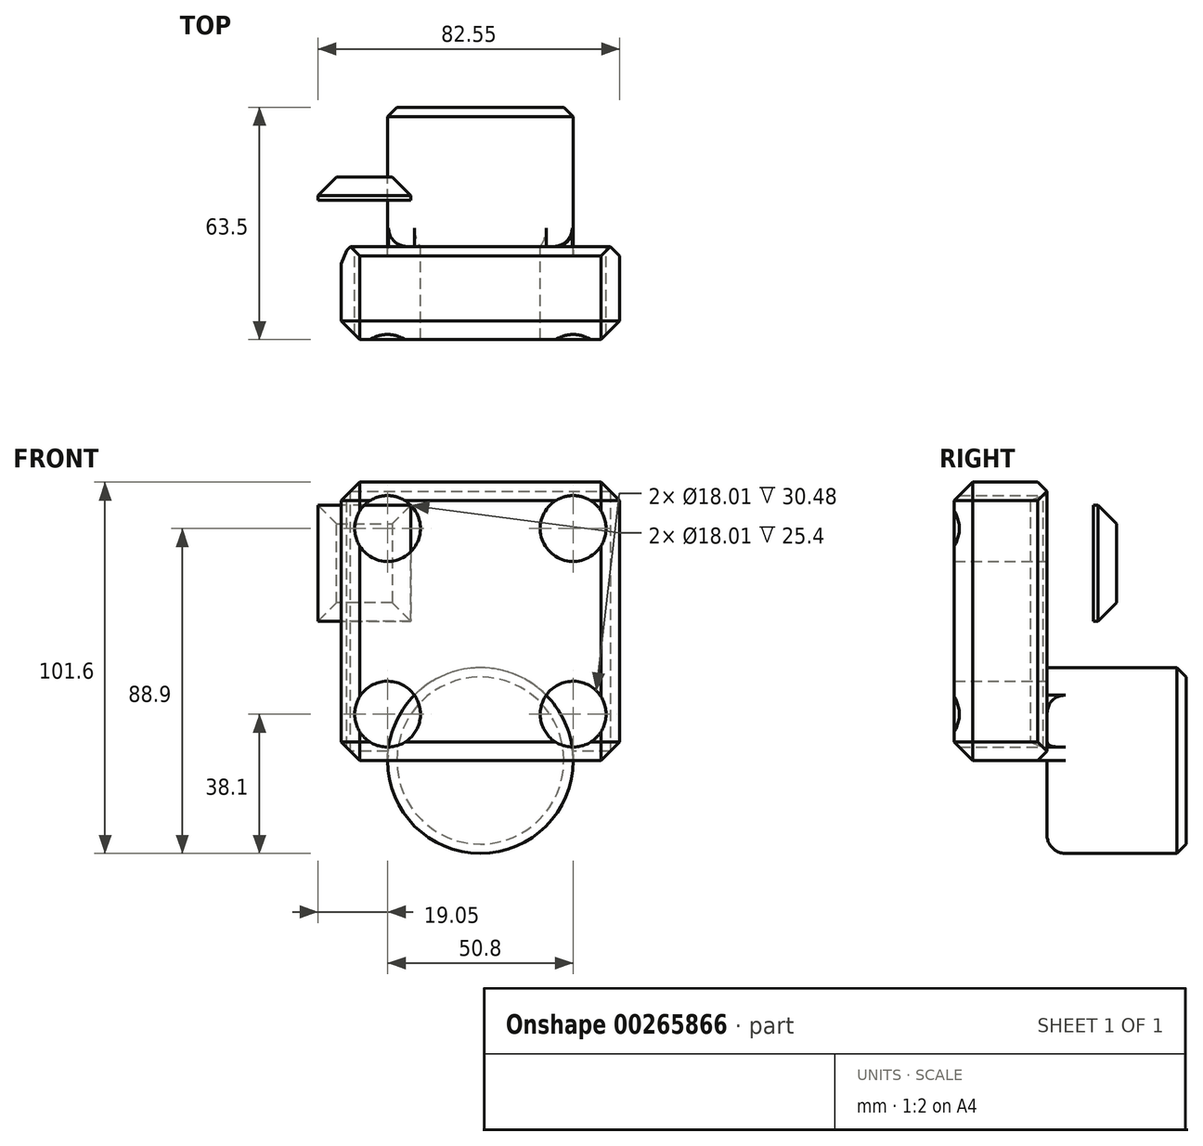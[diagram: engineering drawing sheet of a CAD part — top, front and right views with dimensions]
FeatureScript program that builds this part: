
annotation { "Feature Type Name" : "Feature", "Feature Type Description" : "" }
export const myFeature = defineFeature(function(context is Context, id is Id, definition is map)
    precondition{}
    {
        {
            var Q0;
            Q0=qCreatedBy(makeId("Front.planeOp"),FACE);
            var sketch = newSketch(context, id + "F0", { "sketchPlane" : qUnion([Q0])});
            skLineSegment(sketch, "E0.bottom", {"start": v(-38.1, 38.1) * mm, "end": v(38.1, 38.1) * mm});
            skLineSegment(sketch, "E0.top", {"start": v(-38.1, -38.1) * mm, "end": v(38.1, -38.1) * mm});
            skLineSegment(sketch, "E0.left", {"start": v(-38.1, 38.1) * mm, "end": v(-38.1, -38.1) * mm});
            skLineSegment(sketch, "E0.right", {"start": v(38.1, 38.1) * mm, "end": v(38.1, -38.1) * mm});
            skSolve(sketch);
        }
        {
            var Q0;
            Q0=makeQuery(id+"F0.imprint","IMPRINT",FACE,{"disambiguationData":[TD([[makeQuery(id+"F0.imprint","IMPRINT",EDGE,{"derivedFrom":sQuery(id+"F0.wireOp",EDGE,"E0.bottom")}),-1.0]])]});
            extrude(context, id + "F1", {"entities" : qUnion([Q0]), "oppositeDirection" : true, "depth" : 25.4 * mm});
        }
        {
            var Q0;
            Q0=makeQuery(id+"F1.opExtrude","CAP_FACE",FACE,{"disambiguationData":[OSD([sQuery(id+"F0.wireOp",EDGE,"E0.bottom"),sQuery(id+"F0.wireOp",EDGE,"E0.top"),sQuery(id+"F0.wireOp",EDGE,"E0.left"),sQuery(id+"F0.wireOp",EDGE,"E0.right")])],"isStart":false});
            var sketch = newSketch(context, id + "F2", { "sketchPlane" : qUnion([Q0])});
            skCircle(sketch, "E1", {"center": v(25.4, -25.4) * mm, "radius": 9 * mm});
            skCircle(sketch, "E2", {"center": v(-25.4, -25.4) * mm, "radius": 9 * mm});
            skCircle(sketch, "E3", {"center": v(25.4, 25.4) * mm, "radius": 9 * mm});
            skCircle(sketch, "E4", {"center": v(-25.4, 25.4) * mm, "radius": 9 * mm});
            skSolve(sketch);
        }
        {
            var Q0;
            Q0 = qSketchRegion(id + "F2", true);
            extrude(context, id + "F3", {"entities" : qUnion([Q0]), "operationType" : NewBodyOperationType.REMOVE, "oppositeDirection" : true, "depth" : 25.4 * mm});
        }
        {
            var Q0;
            Q0=makeQuery(id+"F1.opExtrude","SWEPT_FACE",FACE,{"disambiguationData":[OSD([sQuery(id+"F0.wireOp",EDGE,"E0.top")])]});
            var sketch = newSketch(context, id + "F4", { "sketchPlane" : qUnion([Q0])});
            skLineSegment(sketch, "E5.bottom", {"start": v(0, -63.5) * mm, "end": v(-25.4, -63.5) * mm});
            skLineSegment(sketch, "E5.top", {"start": v(0, -25.4) * mm, "end": v(-25.4, -25.4) * mm});
            skLineSegment(sketch, "E5.left", {"start": v(0, -63.5) * mm, "end": v(0, -25.4) * mm});
            skLineSegment(sketch, "E5.right", {"start": v(-25.4, -63.5) * mm, "end": v(-25.4, -25.4) * mm});
            skSolve(sketch);
        }
        {
            var Q0;
            Q0=makeQuery(id+"F4.imprint","IMPRINT",FACE,{"disambiguationData":[TD([[makeQuery(id+"F4.imprint","IMPRINT",EDGE,{"derivedFrom":sQuery(id+"F4.wireOp",EDGE,"E5.bottom")}),-1.0]])]});
            var Q1;
            Q1=sQuery(id+"F4.wireOp",EDGE,"E5.left");
            revolve(context, id + "F5", {"operationType" : NewBodyOperationType.ADD, "entities" : qUnion([Q0]), "axis" : qUnion([Q1]), "revolveType" : RevolveType.FULL});
        }
        {
            var Q0;
            Q0=qCreatedBy(makeId("Top.planeOp"),FACE);
            var sketch = newSketch(context, id + "F6", { "sketchPlane" : qUnion([Q0])});
            skLineSegment(sketch, "E6.bottom", {"start": v(-19.05, 44.45) * mm, "end": v(-44.45, 44.45) * mm});
            skLineSegment(sketch, "E6.top", {"start": v(-19.05, 38.1) * mm, "end": v(-44.45, 38.1) * mm});
            skLineSegment(sketch, "E6.left", {"start": v(-19.05, 44.45) * mm, "end": v(-19.05, 38.1) * mm});
            skLineSegment(sketch, "E6.right", {"start": v(-44.45, 44.45) * mm, "end": v(-44.45, 38.1) * mm});
            skSolve(sketch);
        }
        {
            var Q0;
            Q0 = qSketchRegion(id + "F6", true);
            extrude(context, id + "F7", {"entities" : qUnion([Q0]), "depth" : 31.75 * mm});
        }
        {
            var Q0;
            Q0=makeQuery(id+"F1.opExtrude","CAP_EDGE",EDGE,{"disambiguationData":[OSD([sQuery(id+"F0.wireOp",EDGE,"E0.right")])],"isStart":false});
            var Q1;
            Q1=makeQuery(id+"F1.opExtrude","CAP_EDGE",EDGE,{"disambiguationData":[OSD([sQuery(id+"F0.wireOp",EDGE,"E0.bottom")])],"isStart":false});
            var Q2;
            Q2=makeQuery(id+"F1.opExtrude","CAP_EDGE",EDGE,{"disambiguationData":[OSD([sQuery(id+"F0.wireOp",EDGE,"E0.left")])],"isStart":false});
            var Q3;
            {var subQ0=sQuery(id+"F0.wireOp",EDGE,"E0.left");var subQ1=sQuery(id+"F0.wireOp",EDGE,"E0.top");var subQ2=makeQuery(id+"F1.opExtrude","SWEPT_FACE",FACE,{"disambiguationData":[OSD([subQ1])]});var subQ3=makeQuery(id+"F1.opExtrude","CAP_FACE",FACE,{"disambiguationData":[OSD([sQuery(id+"F0.wireOp",EDGE,"E0.bottom"),subQ1,subQ0,sQuery(id+"F0.wireOp",EDGE,"E0.right")])],"isStart":false});Q3=makeQuery(id+"F5.boolean.opBoolean","SPLIT",EDGE,{"disambiguationData":[topologyDisambiguationEdgeConnected([subQ3,subQ2]),TD([makeQuery(id+"F1.opExtrude","SWEPT_FACE",FACE,{"disambiguationData":[OSD([subQ0])]})])],"derivedFrom":makeQuery(id+"F1.opExtrude","CAP_EDGE",EDGE,{"disambiguationData":[OSD([subQ1])],"isStart":false})});}
            var Q4;
            {var subQ0=sQuery(id+"F0.wireOp",EDGE,"E0.right");var subQ1=sQuery(id+"F0.wireOp",EDGE,"E0.top");var subQ2=makeQuery(id+"F1.opExtrude","SWEPT_FACE",FACE,{"disambiguationData":[OSD([subQ1])]});var subQ3=makeQuery(id+"F1.opExtrude","CAP_FACE",FACE,{"disambiguationData":[OSD([sQuery(id+"F0.wireOp",EDGE,"E0.bottom"),subQ1,sQuery(id+"F0.wireOp",EDGE,"E0.left"),subQ0])],"isStart":false});Q4=makeQuery(id+"F5.boolean.opBoolean","SPLIT",EDGE,{"disambiguationData":[topologyDisambiguationEdgeConnected([subQ3,subQ2]),TD([makeQuery(id+"F1.opExtrude","SWEPT_FACE",FACE,{"disambiguationData":[OSD([subQ0])]})])],"derivedFrom":makeQuery(id+"F1.opExtrude","CAP_EDGE",EDGE,{"disambiguationData":[OSD([subQ1])],"isStart":false})});}
            var Q5;
            Q5=makeQuery(id+"F5.opRevolve","SWEPT_EDGE",EDGE,{"disambiguationData":[OSD([sQuery(id+"F4.wireOp",EDGE,"E5.bottom"),sQuery(id+"F4.wireOp",EDGE,"E5.right")])]});
            chamfer(context, id + "F8", {"entities" : qUnion([Q0, Q1, Q2, Q3, Q4, Q5]), "width" : 2.54 * mm, "tangentPropagation" : true});
        }
        {
            var Q0;
            {var subQ0=sQuery(id+"F4.wireOp",EDGE,"E5.top");var subQ1=sQuery(id+"F0.wireOp",EDGE,"E0.top");var subQ2=makeQuery(id+"F1.opExtrude","CAP_FACE",FACE,{"disambiguationData":[OSD([sQuery(id+"F0.wireOp",EDGE,"E0.bottom"),subQ1,sQuery(id+"F0.wireOp",EDGE,"E0.left"),sQuery(id+"F0.wireOp",EDGE,"E0.right")])],"isStart":false});var subQ3=sQuery(id+"F4.wireOp",EDGE,"E5.right");var subQ4=makeQuery(id+"F5.opRevolve","SWEPT_FACE",FACE,{"disambiguationData":[OSD([subQ3])]});Q0=makeQuery(id+"F5.boolean.opBoolean","SPLIT",EDGE,{"disambiguationData":[topologyDisambiguationEdgeConnected([subQ2,subQ4]),TD([subQ2,makeQuery(id+"F3.boolean.opBoolean","COPY",FACE,{"derivedFrom":makeQuery(id+"F3.opExtrude","SWEPT_FACE",FACE,{"disambiguationData":[OSD([sQuery(id+"F2.wireOp",EDGE,"E1")])]})}),makeQuery(id+"F3.boolean.opBoolean","COPY",FACE,{"derivedFrom":makeQuery(id+"F3.opExtrude","SWEPT_FACE",FACE,{"disambiguationData":[OSD([sQuery(id+"F2.wireOp",EDGE,"E2")])]})}),makeQuery(id+"F5.opRevolve","SWEPT_FACE",FACE,{"disambiguationData":[OSD([subQ0])]}),subQ4])],"derivedFrom":makeQuery(id+"F5.opRevolve","SWEPT_EDGE",EDGE,{"disambiguationData":[OSD([subQ1,subQ0,subQ3])]})});}
            var Q1;
            {var subQ0=sQuery(id+"F0.wireOp",EDGE,"E0.top");Q1=makeQuery(id+"F5.boolean.opBoolean","SPLIT",EDGE,{"disambiguationData":[topologyDisambiguationEdgeConnected([makeQuery(id+"F1.opExtrude","SWEPT_FACE",FACE,{"disambiguationData":[OSD([subQ0])]}),makeQuery(id+"F5.opRevolve","SWEPT_FACE",FACE,{"disambiguationData":[OSD([sQuery(id+"F4.wireOp",EDGE,"E5.top")])]})])],"derivedFrom":makeQuery(id+"F1.opExtrude","CAP_EDGE",EDGE,{"disambiguationData":[OSD([subQ0])],"isStart":false})});}
            fillet(context, id + "F9", {"entities" : qUnion([Q0, Q1]), "radius" : 5.08 * mm, "tangentPropagation" : true, "allowEdgeOverflow" : false});
        }
        {
            var Q0;
            Q0=makeQuery(id+"F7.opExtrude","SWEPT_EDGE",EDGE,{"disambiguationData":[OSD([sQuery(id+"F6.wireOp",EDGE,"E6.bottom"),sQuery(id+"F6.wireOp",EDGE,"E6.right")])]});
            var Q1;
            Q1=makeQuery(id+"F7.opExtrude","CAP_EDGE",EDGE,{"disambiguationData":[OSD([sQuery(id+"F6.wireOp",EDGE,"E6.bottom")])],"isStart":false});
            var Q2;
            Q2=makeQuery(id+"F7.opExtrude","SWEPT_EDGE",EDGE,{"disambiguationData":[OSD([sQuery(id+"F6.wireOp",EDGE,"E6.bottom"),sQuery(id+"F6.wireOp",EDGE,"E6.left")])]});
            var Q3;
            Q3=makeQuery(id+"F7.opExtrude","CAP_EDGE",EDGE,{"disambiguationData":[OSD([sQuery(id+"F6.wireOp",EDGE,"E6.bottom")])],"isStart":true});
            var Q4;
            Q4=makeQuery(id+"F3.boolean.opBoolean","COPY",EDGE,{"derivedFrom":makeQuery(id+"F3.opExtrude","CAP_EDGE",EDGE,{"disambiguationData":[OSD([sQuery(id+"F2.wireOp",EDGE,"E3")])],"isStart":true})});
            var Q5;
            Q5=makeQuery(id+"F3.boolean.opBoolean","COPY",EDGE,{"derivedFrom":makeQuery(id+"F3.opExtrude","CAP_EDGE",EDGE,{"disambiguationData":[OSD([sQuery(id+"F2.wireOp",EDGE,"E4")])],"isStart":true})});
            var Q6;
            {var subQ0=sQuery(id+"F2.wireOp",EDGE,"E2");Q6=makeQuery(id+"F5.boolean.opBoolean","SPLIT",EDGE,{"disambiguationData":[topologyDisambiguationEdgeConnected([makeQuery(id+"F1.opExtrude","CAP_FACE",FACE,{"disambiguationData":[OSD([sQuery(id+"F0.wireOp",EDGE,"E0.bottom"),sQuery(id+"F0.wireOp",EDGE,"E0.top"),sQuery(id+"F0.wireOp",EDGE,"E0.left"),sQuery(id+"F0.wireOp",EDGE,"E0.right")])],"isStart":false})])],"derivedFrom":makeQuery(id+"F3.boolean.opBoolean","COPY",EDGE,{"derivedFrom":makeQuery(id+"F3.opExtrude","CAP_EDGE",EDGE,{"disambiguationData":[OSD([subQ0])],"isStart":true})})});}
            var Q7;
            {var subQ0=sQuery(id+"F2.wireOp",EDGE,"E1");Q7=makeQuery(id+"F5.boolean.opBoolean","SPLIT",EDGE,{"disambiguationData":[topologyDisambiguationEdgeConnected([makeQuery(id+"F1.opExtrude","CAP_FACE",FACE,{"disambiguationData":[OSD([sQuery(id+"F0.wireOp",EDGE,"E0.bottom"),sQuery(id+"F0.wireOp",EDGE,"E0.top"),sQuery(id+"F0.wireOp",EDGE,"E0.left"),sQuery(id+"F0.wireOp",EDGE,"E0.right")])],"isStart":false})])],"derivedFrom":makeQuery(id+"F3.boolean.opBoolean","COPY",EDGE,{"derivedFrom":makeQuery(id+"F3.opExtrude","CAP_EDGE",EDGE,{"disambiguationData":[OSD([subQ0])],"isStart":true})})});}
            chamfer(context, id + "F10", {"entities" : qUnion([Q0, Q1, Q2, Q3, Q4, Q5, Q6, Q7]), "width" : 5.08 * mm, "tangentPropagation" : true});
        }
        {
            var Q0;
            Q0=makeQuery(id+"F1.opExtrude","SWEPT_EDGE",EDGE,{"disambiguationData":[OSD([sQuery(id+"F0.wireOp",EDGE,"E0.bottom"),sQuery(id+"F0.wireOp",EDGE,"E0.right")])]});
            var Q1;
            Q1=makeQuery(id+"F1.opExtrude","SWEPT_EDGE",EDGE,{"disambiguationData":[OSD([sQuery(id+"F0.wireOp",EDGE,"E0.top"),sQuery(id+"F0.wireOp",EDGE,"E0.right")])]});
            var Q2;
            Q2=makeQuery(id+"F1.opExtrude","CAP_EDGE",EDGE,{"disambiguationData":[OSD([sQuery(id+"F0.wireOp",EDGE,"E0.right")])],"isStart":true});
            var Q3;
            Q3=makeQuery(id+"F1.opExtrude","CAP_EDGE",EDGE,{"disambiguationData":[OSD([sQuery(id+"F0.wireOp",EDGE,"E0.bottom")])],"isStart":true});
            var Q4;
            Q4=makeQuery(id+"F1.opExtrude","CAP_EDGE",EDGE,{"disambiguationData":[OSD([sQuery(id+"F0.wireOp",EDGE,"E0.top")])],"isStart":true});
            var Q5;
            Q5=makeQuery(id+"F1.opExtrude","SWEPT_EDGE",EDGE,{"disambiguationData":[OSD([sQuery(id+"F0.wireOp",EDGE,"E0.top"),sQuery(id+"F0.wireOp",EDGE,"E0.left")])]});
            var Q6;
            Q6=makeQuery(id+"F1.opExtrude","SWEPT_EDGE",EDGE,{"disambiguationData":[OSD([sQuery(id+"F0.wireOp",EDGE,"E0.bottom"),sQuery(id+"F0.wireOp",EDGE,"E0.left")])]});
            var Q7;
            Q7=makeQuery(id+"F1.opExtrude","CAP_EDGE",EDGE,{"disambiguationData":[OSD([sQuery(id+"F0.wireOp",EDGE,"E0.left")])],"isStart":true});
            var Q8;
            {var subQ0=sQuery(id+"F0.wireOp",EDGE,"E0.left");Q8=makeQuery(id+"F8.opChamfer","BLEND_EDGE",EDGE,{"blendedFrom":[makeQuery(id+"F1.opExtrude","CAP_EDGE",EDGE,{"disambiguationData":[OSD([subQ0])],"isStart":false}),makeQuery(id+"F1.opExtrude","SWEPT_FACE",FACE,{"disambiguationData":[OSD([subQ0])]})],"blendedInto":[makeQuery(id+"F1.opExtrude","SWEPT_FACE",FACE,{"disambiguationData":[OSD([subQ0])]})]});}
            chamfer(context, id + "F11", {"entities" : qUnion([Q0, Q1, Q2, Q3, Q4, Q5, Q6, Q7, Q8]), "width" : 5.08 * mm, "tangentPropagation" : true});
        }
    });
